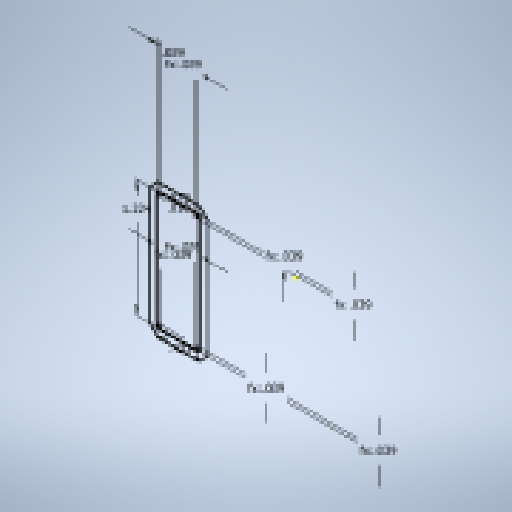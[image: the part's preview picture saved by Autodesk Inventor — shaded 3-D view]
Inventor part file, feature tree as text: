
AUTODESK INVENTOR PART (.ipt)
format: ipt  version: 2024 (Build 280153000, 153)  size: 169,472 bytes
history: native  units: in
note: dims shown in document units (in); Inventor stores cm internally (conversion verified against a paired STEP export)
features: extrude x2, sketch x1
ambient origin geometry x8: Origin, YZ Plane, XZ Plane, XY Plane, X Axis, Y Axis, Z Axis, Center Point
bodies: Solid1 (feature_tree)
feature tree (3):
  sketch  "Sketch1"  dims[d0=1.2244in d1=0.4331in d2=0.0394in d3=0.0394in d4=0.0394in d5=0.0394in d6=0.0394in d7=0.0394in d8=0.0394in d9=0.0394in d10=0.0098in d11=0.0787in d12=0.0591in d13=0.0in d14=0.315in d15=0.0in]
  extrude  "Extrusion1"  Depth=0.0591in TaperAngle=0.0deg
  extrude  "Extrusion2"  Depth=0.315in TaperAngle=0.0deg
